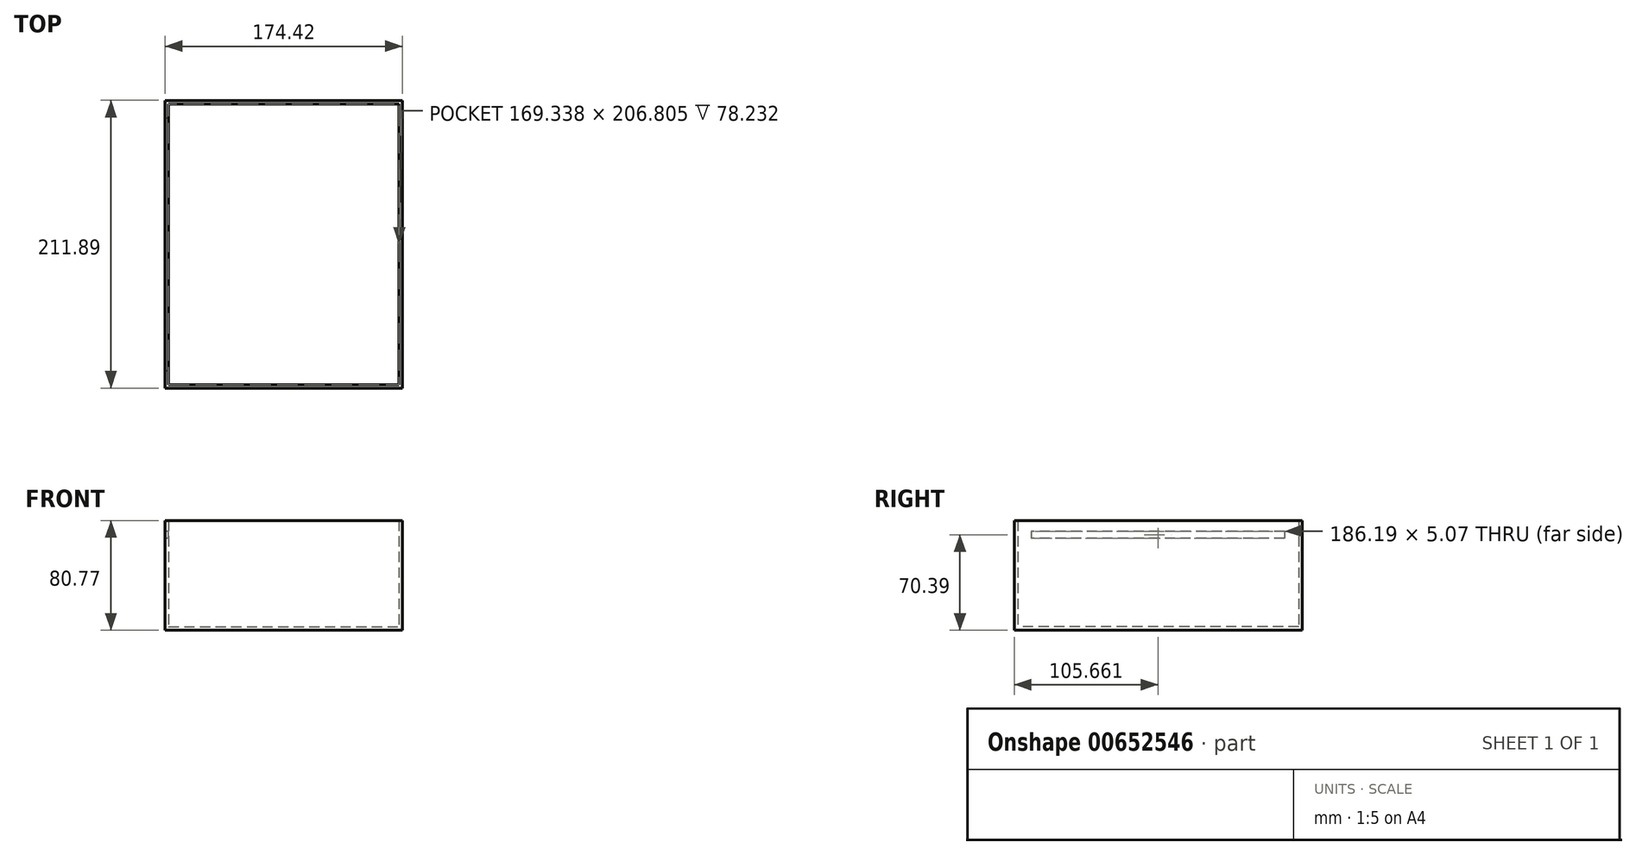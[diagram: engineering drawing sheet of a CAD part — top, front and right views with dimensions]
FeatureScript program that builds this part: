
annotation { "Feature Type Name" : "Feature", "Feature Type Description" : "" }
export const myFeature = defineFeature(function(context is Context, id is Id, definition is map)
    precondition{}
    {
        {
            var Q0;
            Q0=qCreatedBy(makeId("Top.planeOp"),FACE);
            var sketch = newSketch(context, id + "F0", { "sketchPlane" : qUnion([Q0])});
            skLineSegment(sketch, "E0.bottom", {"start": v(-87.84, 107.6) * mm, "end": v(86.58, 107.6) * mm});
            skLineSegment(sketch, "E0.top", {"start": v(-87.84, -104.29) * mm, "end": v(86.58, -104.29) * mm});
            skLineSegment(sketch, "E0.left", {"start": v(-87.84, 107.6) * mm, "end": v(-87.84, -104.29) * mm});
            skLineSegment(sketch, "E0.right", {"start": v(86.58, 107.6) * mm, "end": v(86.58, -104.29) * mm});
            skSolve(sketch);
        }
        {
            var Q0;
            Q0=makeQuery(id+"F0.imprint","IMPRINT",FACE,{"disambiguationData":[TD([[makeQuery(id+"F0.imprint","IMPRINT",EDGE,{"derivedFrom":sQuery(id+"F0.wireOp",EDGE,"E0.bottom")}),-1.0]])]});
            extrude(context, id + "F1", {"entities" : qUnion([Q0]), "depth" : 80.77 * mm, "offsetDistance" : 25.4 * mm});
        }
        {
            var Q0;
            Q0=makeQuery(id+"F1.opExtrude","CAP_FACE",FACE,{"disambiguationData":[OSD([sQuery(id+"F0.wireOp",EDGE,"E0.bottom"),sQuery(id+"F0.wireOp",EDGE,"E0.top"),sQuery(id+"F0.wireOp",EDGE,"E0.left"),sQuery(id+"F0.wireOp",EDGE,"E0.right")])],"isStart":false});
            shell(context, id + "F2", {"entities" : qUnion([Q0]), "thickness" : 2.54 * mm});
        }
        {
            var Q0;
            Q0=makeQuery(id+"F1.opExtrude","SWEPT_FACE",FACE,{"disambiguationData":[OSD([sQuery(id+"F0.wireOp",EDGE,"E0.left")])]});
            var sketch = newSketch(context, id + "F3", { "sketchPlane" : qUnion([Q0])});
            skLineSegment(sketch, "E1.bottom", {"start": v(-94.47, 72.92) * mm, "end": v(91.72, 72.92) * mm});
            skLineSegment(sketch, "E1.top", {"start": v(-94.47, 67.86) * mm, "end": v(91.72, 67.86) * mm});
            skLineSegment(sketch, "E1.left", {"start": v(-94.47, 72.92) * mm, "end": v(-94.47, 67.86) * mm});
            skLineSegment(sketch, "E1.right", {"start": v(91.72, 72.92) * mm, "end": v(91.72, 67.86) * mm});
            skSolve(sketch);
        }
        {
            var Q0;
            Q0=makeQuery(id+"F3.imprint","IMPRINT",FACE,{"disambiguationData":[TD([[makeQuery(id+"F3.imprint","IMPRINT",EDGE,{"derivedFrom":sQuery(id+"F3.wireOp",EDGE,"E1.bottom")}),-1.0]])]});
            extrude(context, id + "F4", {"entities" : qUnion([Q0]), "operationType" : NewBodyOperationType.REMOVE, "oppositeDirection" : true, "depth" : 11.94 * mm, "offsetDistance" : 25.4 * mm});
        }
    });
